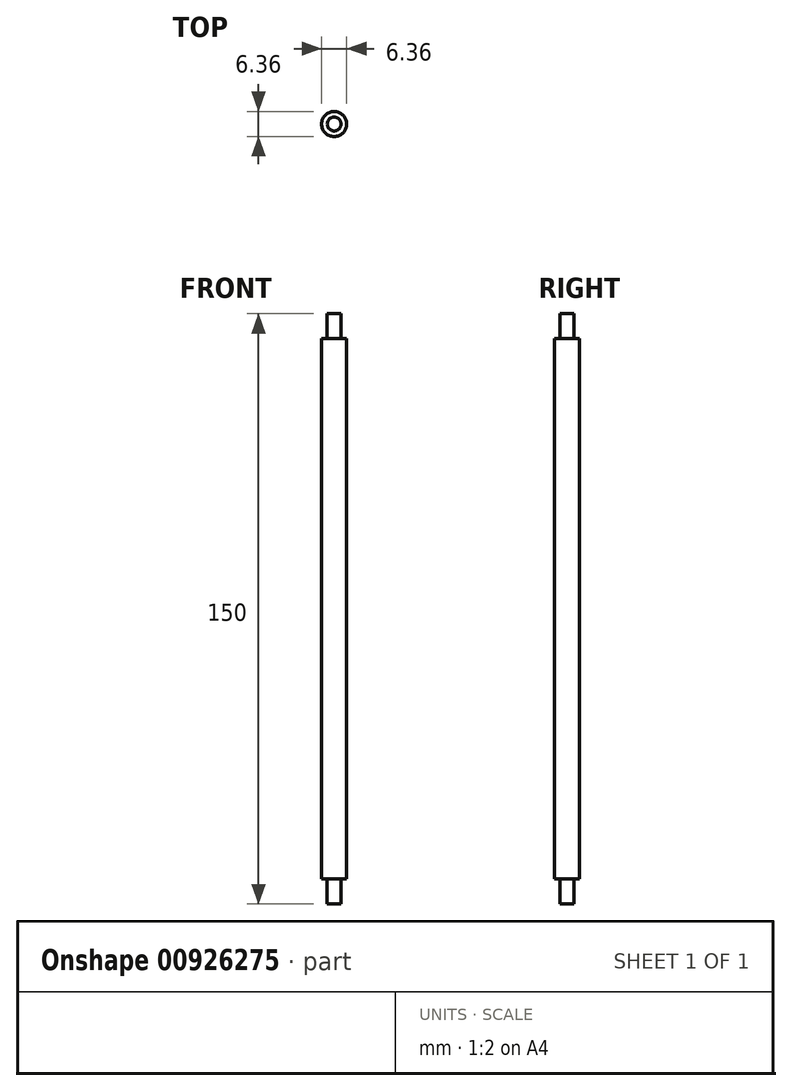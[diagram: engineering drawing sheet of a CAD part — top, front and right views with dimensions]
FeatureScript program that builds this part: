
annotation { "Feature Type Name" : "Feature", "Feature Type Description" : "" }
export const myFeature = defineFeature(function(context is Context, id is Id, definition is map)
    precondition{}
    {
        {
            var Q0;
            Q0=qCreatedBy(makeId("Front.planeOp"),FACE);
            var sketch = newSketch(context, id + "F0", { "sketchPlane" : qUnion([Q0])});
            skLineSegment(sketch, "E0", {"start": v(0, 0) * mm, "end": v(0, 137.3) * mm});
            skLineSegment(sketch, "E1", {"start": v(0, 137.3) * mm, "end": v(0, 143.65) * mm});
            skLineSegment(sketch, "E2", {"start": v(0, 143.65) * mm, "end": v(1.75, 143.65) * mm});
            skLineSegment(sketch, "E3", {"start": v(1.75, 143.65) * mm, "end": v(1.75, 137.3) * mm});
            skLineSegment(sketch, "E4", {"start": v(1.75, 137.3) * mm, "end": v(3.17, 137.3) * mm});
            skLineSegment(sketch, "E5", {"start": v(0, 68.65) * mm, "end": v(23.41, 68.65) * mm, "construction": true});
            skLineSegment(sketch, "E6", {"start": v(3.17, 137.3) * mm, "end": v(3.17, 68.65) * mm});
            skLineSegment(sketch, "E7.MirrorCS", {"start": v(0, -6.35) * mm, "end": v(1.75, -6.35) * mm});
            skLineSegment(sketch, "E8.MirrorCS", {"start": v(1.75, -6.35) * mm, "end": v(1.75, 0) * mm});
            skLineSegment(sketch, "E9.MirrorCS", {"start": v(1.75, 0) * mm, "end": v(3.17, 0) * mm});
            skLineSegment(sketch, "E10.MirrorCS", {"start": v(3.17, 0) * mm, "end": v(3.17, 68.65) * mm});
            skLineSegment(sketch, "E11.MirrorCS", {"start": v(0, 0) * mm, "end": v(0, -6.35) * mm});
            skSolve(sketch);
        }
        {
            var Q0;
            Q0=makeQuery(id+"F0.imprint","IMPRINT",FACE,{"disambiguationData":[TD([[makeQuery(id+"F0.imprint","IMPRINT",EDGE,{"derivedFrom":sQuery(id+"F0.wireOp",EDGE,"E0")}),-1.0]])]});
            var Q1;
            Q1=sQuery(id+"F0.wireOp",EDGE,"E0");
            revolve(context, id + "F1", {"surfaceOperationType" : NewSurfaceOperationType.NEW, "entities" : qUnion([Q0]), "axis" : qUnion([Q1]), "revolveType" : RevolveType.FULL});
        }
    });
